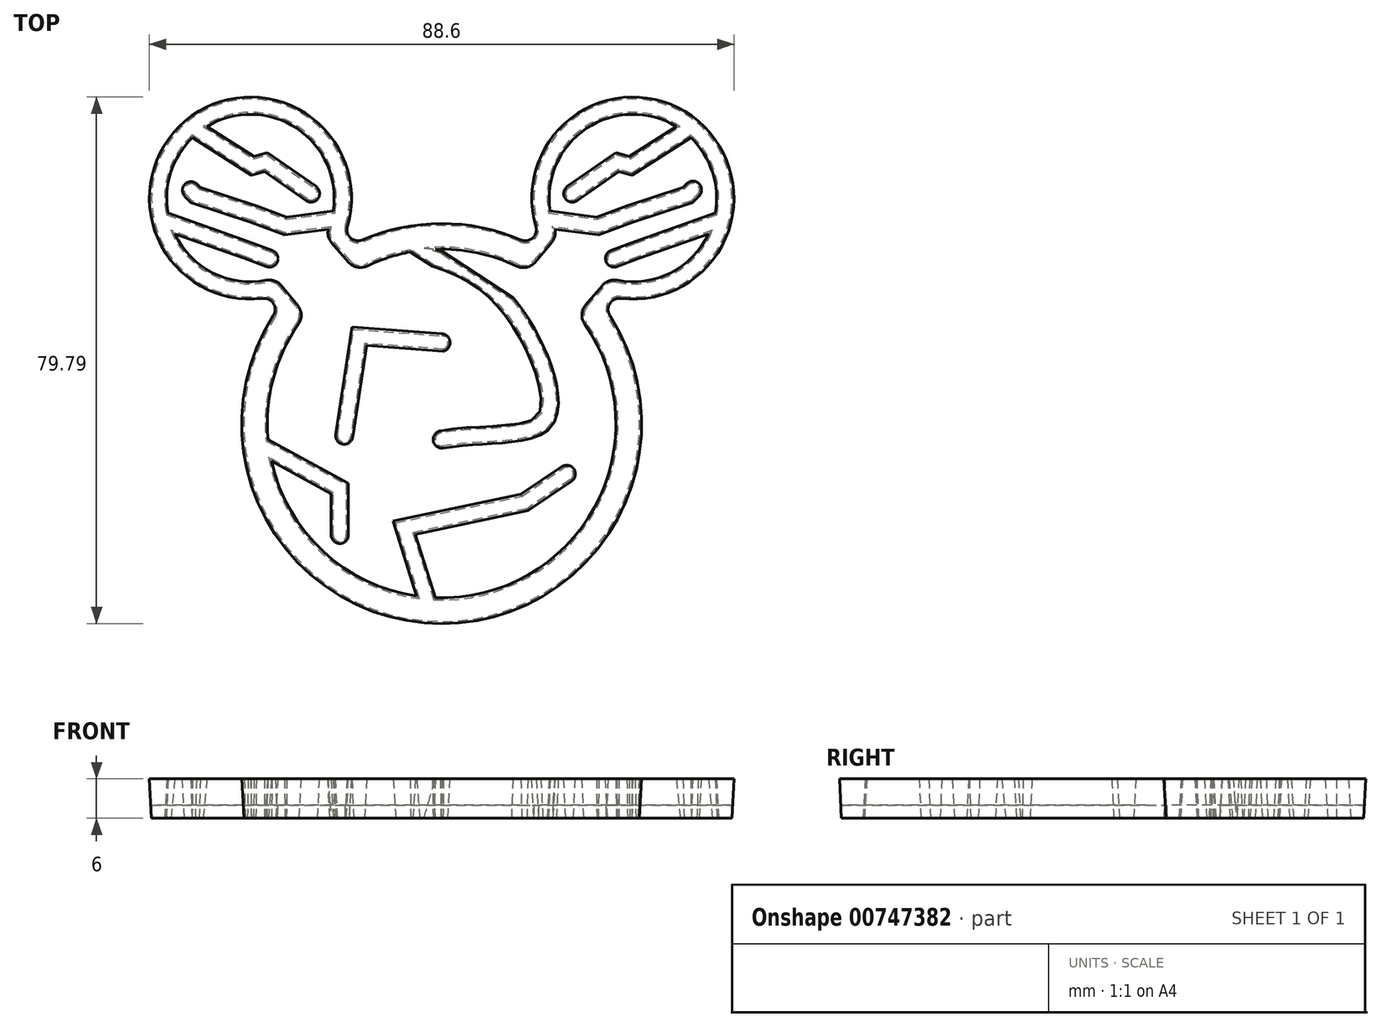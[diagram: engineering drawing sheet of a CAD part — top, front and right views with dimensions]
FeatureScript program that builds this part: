
annotation { "Feature Type Name" : "Feature", "Feature Type Description" : "" }
export const myFeature = defineFeature(function(context is Context, id is Id, definition is map)
    precondition{}
    {
        {
            var Q0;
            Q0=qCreatedBy(makeId("Top.planeOp"),FACE);
            var sketch = newSketch(context, id + "F0", { "sketchPlane" : qUnion([Q0])});
            skArc(sketch, "E0", {"start": v(-25.24, 16.21) * mm, "mid": v(-0.03, -30) * mm, "end": v(25.28, 16.16) * mm});
            skArc(sketch, "E1.0", {"start": v(-4.68, 26.33) * mm, "mid": v(-8.15, 25.47) * mm, "end": v(-11.47, 24.15) * mm});
            skPoint(sketch, "E2.second.point", {"position": v(-37.14, 46.76) * mm});
            skArc(sketch, "E3", {"start": v(-14.6, 29.95) * mm, "mid": v(-38.69, 45.6) * mm, "end": v(-27.17, 19.28) * mm});
            skPoint(sketch, "E3.third.point", {"position": v(-14.84, 29.18) * mm});
            skArc(sketch, "E4", {"start": v(17.02, 24.7) * mm, "mid": v(17.1, 24.65) * mm, "end": v(17.16, 24.6) * mm});
            skArc(sketch, "E5.0", {"start": v(-37.82, 43.7) * mm, "mid": v(-41.35, 38.19) * mm, "end": v(-41.74, 31.65) * mm});
            skPoint(sketch, "E6.7.internal.orphan", {"position": v(-28.98, 27.82) * mm});
            skPoint(sketch, "E6.8.internal.orphan", {"position": v(-28.98, 27.62) * mm});
            skPoint(sketch, "E6.9.internal.orphan", {"position": v(-28.98, 27.72) * mm});
            skLineSegment(sketch, "E7", {"start": v(-36.16, 45.01) * mm, "end": v(-28.5, 40.12) * mm});
            skLineSegment(sketch, "E8", {"start": v(-28.5, 40.12) * mm, "end": v(-26.48, 40.72) * mm});
            skLineSegment(sketch, "E9", {"start": v(-26.48, 40.72) * mm, "end": v(-19.25, 35.69) * mm});
            skLineSegment(sketch, "E10.0", {"start": v(-26.83, 38.53) * mm, "end": v(-20.39, 34.04) * mm});
            skLineSegment(sketch, "E10.1", {"start": v(-28.8, 37.94) * mm, "end": v(-26.83, 38.53) * mm});
            skLineSegment(sketch, "E10.2", {"start": v(-31.42, 39.61) * mm, "end": v(-28.8, 37.94) * mm});
            skArc(sketch, "E11", {"start": v(-20.39, 34.04) * mm, "mid": v(-19, 34.3) * mm, "end": v(-19.25, 35.69) * mm});
            skLineSegment(sketch, "E12", {"start": v(-16.18, 31.93) * mm, "end": v(-23.53, 30.95) * mm});
            skLineSegment(sketch, "E13", {"start": v(-23.53, 30.95) * mm, "end": v(-28.18, 32.7) * mm});
            skLineSegment(sketch, "E14", {"start": v(-41.74, 31.65) * mm, "end": v(-29.44, 27.32) * mm});
            skLineSegment(sketch, "E15.1", {"start": v(-41.03, 29.28) * mm, "end": v(-29.78, 25.32) * mm});
            skLineSegment(sketch, "E16", {"start": v(-31.42, 39.61) * mm, "end": v(-37.82, 43.7) * mm});
            skArc(sketch, "E17.trimOffspring", {"start": v(-16.18, 31.93) * mm, "mid": v(-21.86, 45.04) * mm, "end": v(-36.16, 45.01) * mm});
            skArc(sketch, "E18.trimOffspring", {"start": v(-41.03, 29.28) * mm, "mid": v(-35.17, 22.74) * mm, "end": v(-26.49, 21.41) * mm});
            skArc(sketch, "E19.cCircle", {"start": v(-4.68, 26.33) * mm, "mid": v(-8.15, 25.47) * mm, "end": v(-11.47, 24.15) * mm, "construction": true});
            skPoint(sketch, "E19.0.start.orphan", {"position": v(0, 26.74) * mm});
            skFitSpline(sketch, "E20", {"points": [v(-2.69, 26.6) * mm, v(12.72, 16) * mm, v(16.58, 0) * mm, v(0.19, -3.4) * mm], "startDerivative": vector(62.23, -17.29) * mm, "endDerivative": vector(-64.8, -10.15) * mm});
            skFitSpline(sketch, "E21.0", {"points": [v(-3.22, 24.68) * mm, v(-1.98, 24.33) * mm, v(0.32, 23.58) * mm, v(3.28, 22.25) * mm, v(5.82, 20.66) * mm, v(7.67, 19.08) * mm, v(9.04, 17.61) * mm, v(10.03, 16.4) * mm, v(10.97, 15.07) * mm, v(11.88, 13.6) * mm, v(12.73, 12.04) * mm, v(13.5, 10.42) * mm, v(14.17, 8.8) * mm, v(14.72, 7.19) * mm, v(15.11, 5.66) * mm, v(15.35, 4.24) * mm, v(15.4, 3) * mm, v(15.32, 2.18) * mm, v(15.18, 1.66) * mm, v(15.06, 1.35) * mm, v(14.92, 1.1) * mm, v(14.71, 0.85) * mm, v(14.34, 0.53) * mm, v(13.58, 0.15) * mm, v(12.52, -0.16) * mm, v(11.19, -0.4) * mm, v(9.64, -0.58) * mm, v(7.34, -0.75) * mm, v(4.1, -0.92) * mm, v(1.3, -1.2) * mm, v(-0.12, -1.42) * mm]});
            skLineSegment(sketch, "E22", {"start": v(9.33, 17.24) * mm, "end": v(-4.68, 26.33) * mm});
            skArc(sketch, "E23", {"start": v(-0.12, -1.42) * mm, "mid": v(-0.95, -2.57) * mm, "end": v(0.19, -3.4) * mm});
            skLineSegment(sketch, "E24", {"start": v(-3.33, -26.53) * mm, "end": v(-6.94, -15.03) * mm});
            skLineSegment(sketch, "E25", {"start": v(-6.94, -15.03) * mm, "end": v(12.14, -11.02) * mm});
            skLineSegment(sketch, "E26", {"start": v(12.14, -11.02) * mm, "end": v(18.4, -6.8) * mm});
            skLineSegment(sketch, "E27.0", {"start": v(12.93, -12.9) * mm, "end": v(19.52, -8.45) * mm});
            skLineSegment(sketch, "E27.1", {"start": v(-4.38, -16.54) * mm, "end": v(12.93, -12.9) * mm});
            skLineSegment(sketch, "E27.2", {"start": v(-1.18, -26.71) * mm, "end": v(-4.38, -16.54) * mm});
            skArc(sketch, "E28", {"start": v(18.4, -6.8) * mm, "mid": v(19.79, -7.07) * mm, "end": v(19.52, -8.45) * mm});
            skLineSegment(sketch, "E29", {"start": v(0, 13.3) * mm, "end": v(-13.35, 14.27) * mm});
            skLineSegment(sketch, "E30", {"start": v(-13.35, 14.27) * mm, "end": v(-15.77, -1.66) * mm});
            skLineSegment(sketch, "E31.0", {"start": v(-11.65, 12.14) * mm, "end": v(-13.8, -1.96) * mm});
            skLineSegment(sketch, "E31.1", {"start": v(0.22, 11.28) * mm, "end": v(-11.65, 12.14) * mm});
            skArc(sketch, "E32", {"start": v(-15.77, -1.66) * mm, "mid": v(-14.93, -2.8) * mm, "end": v(-13.8, -1.96) * mm});
            skArc(sketch, "E33", {"start": v(0, 13.3) * mm, "mid": v(0.95, 12.38) * mm, "end": v(0.22, 11.28) * mm});
            skLineSegment(sketch, "E34", {"start": v(-26.6, -2.63) * mm, "end": v(-14.45, -9.24) * mm});
            skLineSegment(sketch, "E35", {"start": v(-14.45, -9.24) * mm, "end": v(-14.45, -16.87) * mm});
            skLineSegment(sketch, "E36.0", {"start": v(-16.45, -10.43) * mm, "end": v(-16.45, -16.87) * mm});
            skLineSegment(sketch, "E36.1", {"start": v(-26.25, -5.1) * mm, "end": v(-16.45, -10.43) * mm});
            skArc(sketch, "E37", {"start": v(-16.45, -16.87) * mm, "mid": v(-15.45, -17.87) * mm, "end": v(-14.45, -16.87) * mm});
            skArc(sketch, "E38.trimOffspring", {"start": v(-1.18, -26.71) * mm, "mid": v(23.43, -12.9) * mm, "end": v(21.93, 15.3) * mm, "construction": true});
            skArc(sketch, "E39.trimOffspring", {"start": v(-1.18, -26.71) * mm, "mid": v(23.43, -12.9) * mm, "end": v(21.93, 15.3) * mm});
            skArc(sketch, "E40.trimOffspring", {"start": v(-26.25, -5.1) * mm, "mid": v(-18.26, -19.53) * mm, "end": v(-3.33, -26.53) * mm, "construction": true});
            skArc(sketch, "E41.trimOffspring", {"start": v(-26.25, -5.1) * mm, "mid": v(-18.26, -19.53) * mm, "end": v(-3.33, -26.53) * mm});
            skArc(sketch, "E42.filletArc", {"start": v(-25.24, 16.21) * mm, "mid": v(-25.23, 18.36) * mm, "end": v(-27.17, 19.28) * mm});
            skArc(sketch, "E43.filletArc", {"start": v(-14.6, 29.95) * mm, "mid": v(-14, 27.89) * mm, "end": v(-11.88, 27.55) * mm});
            skArc(sketch, "E44.trimOffspring", {"start": v(17.16, 24.6) * mm, "mid": v(17.1, 24.65) * mm, "end": v(17.02, 24.7) * mm});
            skArc(sketch, "E45.trimOffspring", {"start": v(11.82, 27.57) * mm, "mid": v(-0.03, 30) * mm, "end": v(-11.88, 27.55) * mm});
            skPoint(sketch, "E46.orphan", {"position": v(0, 74.82) * mm});
            skPoint(sketch, "E47.end.orphan", {"position": v(-13.16, 0) * mm});
            skPoint(sketch, "E48.end.orphan", {"position": v(0.03, 3.37) * mm});
            skPoint(sketch, "E48.start.orphan", {"position": v(0.03, 5.7) * mm});
            skLineSegment(sketch, "E49", {"start": v(-28.18, 32.7) * mm, "end": v(-36.77, 35.52) * mm});
            skLineSegment(sketch, "E50", {"start": v(-36.77, 35.52) * mm, "end": v(-37.37, 36.13) * mm});
            skLineSegment(sketch, "E51.0", {"start": v(-37.85, 33.77) * mm, "end": v(-38.7, 34.62) * mm});
            skLineSegment(sketch, "E51.1", {"start": v(-28.85, 30.8) * mm, "end": v(-37.85, 33.77) * mm});
            skLineSegment(sketch, "E51.2", {"start": v(-23.76, 28.9) * mm, "end": v(-28.85, 30.8) * mm});
            skLineSegment(sketch, "E51.3", {"start": v(-16.73, 29.84) * mm, "end": v(-23.76, 28.9) * mm});
            skArc(sketch, "E52", {"start": v(-38.7, 34.62) * mm, "mid": v(-38.73, 36) * mm, "end": v(-37.37, 36.13) * mm});
            skLineSegment(sketch, "E53", {"start": v(-29.44, 27.32) * mm, "end": v(-25.8, 25.95) * mm});
            skLineSegment(sketch, "E54", {"start": v(-29.78, 25.32) * mm, "end": v(-26.46, 24.07) * mm});
            skLineSegment(sketch, "E55", {"start": v(-26.46, 24.07) * mm, "end": v(-26.32, 24.43) * mm});
            skArc(sketch, "E56", {"start": v(-26.46, 24.07) * mm, "mid": v(-25.16, 24.67) * mm, "end": v(-25.8, 25.95) * mm});
            skArc(sketch, "E57.MirrorCS", {"start": v(14.6, 29.95) * mm, "mid": v(38.69, 45.6) * mm, "end": v(27.17, 19.28) * mm});
            skArc(sketch, "E58.MirrorCS", {"start": v(16.18, 31.93) * mm, "mid": v(21.86, 45.04) * mm, "end": v(36.16, 45.01) * mm});
            skArc(sketch, "E59.MirrorCS", {"start": v(37.82, 43.7) * mm, "mid": v(41.35, 38.19) * mm, "end": v(41.74, 31.65) * mm});
            skArc(sketch, "E60.MirrorCS", {"start": v(41.03, 29.28) * mm, "mid": v(35.18, 22.74) * mm, "end": v(26.5, 21.4) * mm});
            skArc(sketch, "E61.MirrorCS", {"start": v(25.24, 16.21) * mm, "mid": v(25.23, 18.36) * mm, "end": v(27.17, 19.28) * mm});
            skArc(sketch, "E62.MirrorCS", {"start": v(14.6, 29.95) * mm, "mid": v(14, 27.89) * mm, "end": v(11.88, 27.55) * mm});
            skLineSegment(sketch, "E63.MirrorCS", {"start": v(41.03, 29.28) * mm, "end": v(29.78, 25.32) * mm});
            skLineSegment(sketch, "E64.MirrorCS", {"start": v(41.74, 31.65) * mm, "end": v(29.44, 27.32) * mm});
            skLineSegment(sketch, "E65.MirrorCS", {"start": v(29.44, 27.32) * mm, "end": v(25.8, 25.95) * mm});
            skLineSegment(sketch, "E66.MirrorCS", {"start": v(29.78, 25.32) * mm, "end": v(26.46, 24.07) * mm});
            skLineSegment(sketch, "E67.MirrorCS", {"start": v(28.85, 30.8) * mm, "end": v(37.85, 33.77) * mm});
            skLineSegment(sketch, "E68.MirrorCS", {"start": v(28.18, 32.7) * mm, "end": v(36.77, 35.52) * mm});
            skLineSegment(sketch, "E69.MirrorCS", {"start": v(23.53, 30.95) * mm, "end": v(28.18, 32.7) * mm});
            skLineSegment(sketch, "E70.MirrorCS", {"start": v(23.76, 28.9) * mm, "end": v(28.85, 30.8) * mm});
            skLineSegment(sketch, "E71.MirrorCS", {"start": v(16.73, 29.84) * mm, "end": v(23.76, 28.9) * mm});
            skLineSegment(sketch, "E72.MirrorCS", {"start": v(16.18, 31.93) * mm, "end": v(23.53, 30.95) * mm});
            skLineSegment(sketch, "E73.MirrorCS", {"start": v(26.83, 38.53) * mm, "end": v(20.39, 34.04) * mm});
            skLineSegment(sketch, "E74.MirrorCS", {"start": v(26.48, 40.72) * mm, "end": v(19.25, 35.69) * mm});
            skLineSegment(sketch, "E75.MirrorCS", {"start": v(28.5, 40.12) * mm, "end": v(26.48, 40.72) * mm});
            skLineSegment(sketch, "E76.MirrorCS", {"start": v(28.8, 37.94) * mm, "end": v(26.83, 38.53) * mm});
            skLineSegment(sketch, "E77.MirrorCS", {"start": v(31.42, 39.61) * mm, "end": v(28.8, 37.94) * mm});
            skLineSegment(sketch, "E78.MirrorCS", {"start": v(36.16, 45.01) * mm, "end": v(28.5, 40.12) * mm});
            skLineSegment(sketch, "E79.MirrorCS", {"start": v(31.42, 39.61) * mm, "end": v(37.82, 43.7) * mm});
            skLineSegment(sketch, "E80.MirrorCS", {"start": v(37.85, 33.77) * mm, "end": v(38.7, 34.62) * mm});
            skLineSegment(sketch, "E81.MirrorCS", {"start": v(36.77, 35.52) * mm, "end": v(37.37, 36.13) * mm});
            skArc(sketch, "E82", {"start": v(19.25, 35.69) * mm, "mid": v(19, 34.3) * mm, "end": v(20.39, 34.04) * mm});
            skArc(sketch, "E83", {"start": v(37.37, 36.13) * mm, "mid": v(38.84, 36.09) * mm, "end": v(38.7, 34.62) * mm});
            skArc(sketch, "E84", {"start": v(25.8, 25.95) * mm, "mid": v(25.2, 24.69) * mm, "end": v(26.46, 24.07) * mm});
            skLineSegment(sketch, "E85", {"start": v(16.45, 27.65) * mm, "end": v(13.9, 24.65) * mm});
            skLineSegment(sketch, "E86.MirrorCS", {"start": v(24.6, 20.74) * mm, "end": v(22.05, 17.73) * mm});
            skArc(sketch, "E87.trimOffspring", {"start": v(16.8, 29.64) * mm, "mid": v(16.76, 29.74) * mm, "end": v(16.73, 29.84) * mm});
            skArc(sketch, "E88.trimOffspring", {"start": v(11.51, 24.13) * mm, "mid": v(4.58, 26.34) * mm, "end": v(-2.69, 26.6) * mm, "construction": true});
            skArc(sketch, "E89.trimOffspring", {"start": v(11.51, 24.13) * mm, "mid": v(4.58, 26.34) * mm, "end": v(-2.69, 26.6) * mm});
            skPoint(sketch, "E90.visualSharp", {"position": v(17.24, 28.59) * mm});
            skArc(sketch, "E90.filletArc", {"start": v(16.45, 27.65) * mm, "mid": v(16.9, 28.6) * mm, "end": v(16.8, 29.64) * mm});
            skPoint(sketch, "E91.visualSharp", {"position": v(12.87, 23.44) * mm});
            skArc(sketch, "E91.filletArc", {"start": v(11.51, 24.13) * mm, "mid": v(12.8, 23.98) * mm, "end": v(13.9, 24.65) * mm});
            skArc(sketch, "E92.MirrorCS", {"start": v(21.93, 15.3) * mm, "mid": v(21.58, 16.53) * mm, "end": v(22.05, 17.73) * mm});
            skArc(sketch, "E93.MirrorCS", {"start": v(24.6, 20.74) * mm, "mid": v(25.46, 21.33) * mm, "end": v(26.5, 21.4) * mm});
            skPoint(sketch, "E94.orphan", {"position": v(25.4, 21.68) * mm});
            skPoint(sketch, "E95.orphan", {"position": v(21.02, 16.52) * mm});
            skLineSegment(sketch, "E96", {"start": v(-24.56, 20.72) * mm, "end": v(-22.05, 17.67) * mm});
            skArc(sketch, "E97.trimOffspring", {"start": v(-16.8, 29.63) * mm, "mid": v(-16.77, 29.73) * mm, "end": v(-16.73, 29.84) * mm});
            skArc(sketch, "E98.trimOffspring", {"start": v(-21.96, 15.26) * mm, "mid": v(-25.88, 6.73) * mm, "end": v(-26.6, -2.63) * mm, "construction": true});
            skArc(sketch, "E99.trimOffspring", {"start": v(-21.96, 15.26) * mm, "mid": v(-25.88, 6.73) * mm, "end": v(-26.6, -2.63) * mm});
            skPoint(sketch, "E100.visualSharp", {"position": v(-25.36, 21.69) * mm});
            skArc(sketch, "E100.filletArc", {"start": v(-24.56, 20.72) * mm, "mid": v(-25.43, 21.33) * mm, "end": v(-26.49, 21.41) * mm});
            skPoint(sketch, "E101.visualSharp", {"position": v(-21.07, 16.47) * mm});
            skArc(sketch, "E101.filletArc", {"start": v(-21.96, 15.26) * mm, "mid": v(-21.6, 16.48) * mm, "end": v(-22.05, 17.67) * mm});
            skPoint(sketch, "E102.visualSharp", {"position": v(-17.26, 28.55) * mm});
            skPoint(sketch, "E103.visualSharp", {"position": v(-12.81, 23.47) * mm});
            skArc(sketch, "E104.MirrorCS", {"start": v(-16.44, 27.61) * mm, "mid": v(-16.9, 28.57) * mm, "end": v(-16.8, 29.63) * mm});
            skArc(sketch, "E105.MirrorCS", {"start": v(-11.47, 24.15) * mm, "mid": v(-12.74, 24) * mm, "end": v(-13.84, 24.64) * mm});
            skLineSegment(sketch, "E106.MirrorCS", {"start": v(-16.44, 27.61) * mm, "end": v(-13.84, 24.64) * mm});
            skLineSegment(sketch, "E107", {"start": v(0, 25.77) * mm, "end": v(11.6, 18.2) * mm});
            skLineSegment(sketch, "E108", {"start": v(11.6, 18.2) * mm, "end": v(13.1, 15.43) * mm});
            skLineSegment(sketch, "E109", {"start": v(25.24, 16.21) * mm, "end": v(25.28, 16.16) * mm});
            skPoint(sketch, "E110.MirrorCS.end.orphan", {"position": v(26.7, 21.37) * mm});
            skLineSegment(sketch, "E111", {"start": v(11.82, 27.57) * mm, "end": v(11.88, 27.55) * mm});
            skPoint(sketch, "E112.orphan", {"position": v(0, 5.7) * mm});
            skSolve(sketch);
        }
        {
            var Q0;
            Q0=makeQuery(id+"F0.imprint","IMPRINT",FACE,{"disambiguationData":[TD([[makeQuery(id+"F0.imprint","IMPRINT",EDGE,{"derivedFrom":sQuery(id+"F0.wireOp",EDGE,"E0")}),1.0]])]});
            var Q1;
            Q1=makeQuery(id+"F0.imprint","IMPRINT",FACE,{"disambiguationData":[TD([[makeQuery(id+"F0.imprint","IMPRINT",EDGE,{"derivedFrom":sQuery(id+"F0.wireOp",EDGE,"E29")}),1.0]])]});
            extrude(context, id + "F1", {"entities" : qUnion([Q0, Q1]), "depth" : 6 * mm, "offsetDistance" : 25 * mm, "hasDraft" : true, "draftAngle" : 3 * degree});
        }
        {
            var Q0;
            Q0=qCreatedBy(makeId("Top.planeOp"),FACE);
            var sketch = newSketch(context, id + "F2", { "sketchPlane" : qUnion([Q0])});
            skArc(sketch, "E113.0", {"start": v(-25.24, 16.21) * mm, "mid": v(-0.03, -30) * mm, "end": v(25.28, 16.16) * mm});
            skArc(sketch, "E114.0", {"start": v(14.6, 29.95) * mm, "mid": v(38.69, 45.6) * mm, "end": v(27.17, 19.28) * mm});
            skArc(sketch, "E115.0", {"start": v(11.82, 27.57) * mm, "mid": v(-0.03, 30) * mm, "end": v(-11.88, 27.55) * mm});
            skArc(sketch, "E116.0", {"start": v(-14.6, 29.95) * mm, "mid": v(-38.69, 45.6) * mm, "end": v(-27.17, 19.28) * mm});
            skArc(sketch, "E117.0", {"start": v(25.24, 16.21) * mm, "mid": v(25.23, 18.36) * mm, "end": v(27.17, 19.28) * mm});
            skLineSegment(sketch, "E118.0", {"start": v(25.24, 16.21) * mm, "end": v(25.28, 16.16) * mm});
            skArc(sketch, "E119.0", {"start": v(14.6, 29.95) * mm, "mid": v(14, 27.89) * mm, "end": v(11.88, 27.55) * mm});
            skLineSegment(sketch, "E120.0", {"start": v(11.82, 27.57) * mm, "end": v(11.88, 27.55) * mm});
            skArc(sketch, "E121.0", {"start": v(-14.6, 29.95) * mm, "mid": v(-14, 27.89) * mm, "end": v(-11.88, 27.55) * mm});
            skArc(sketch, "E122.0", {"start": v(-25.24, 16.21) * mm, "mid": v(-25.23, 18.36) * mm, "end": v(-27.17, 19.28) * mm});
            skSolve(sketch);
        }
        {
            var Q0;
            Q0 = qSketchRegion(id + "F2", true);
            extrude(context, id + "F3", {"entities" : qUnion([Q0]), "depth" : 2 * mm, "offsetDistance" : 25 * mm});
        }
    });
